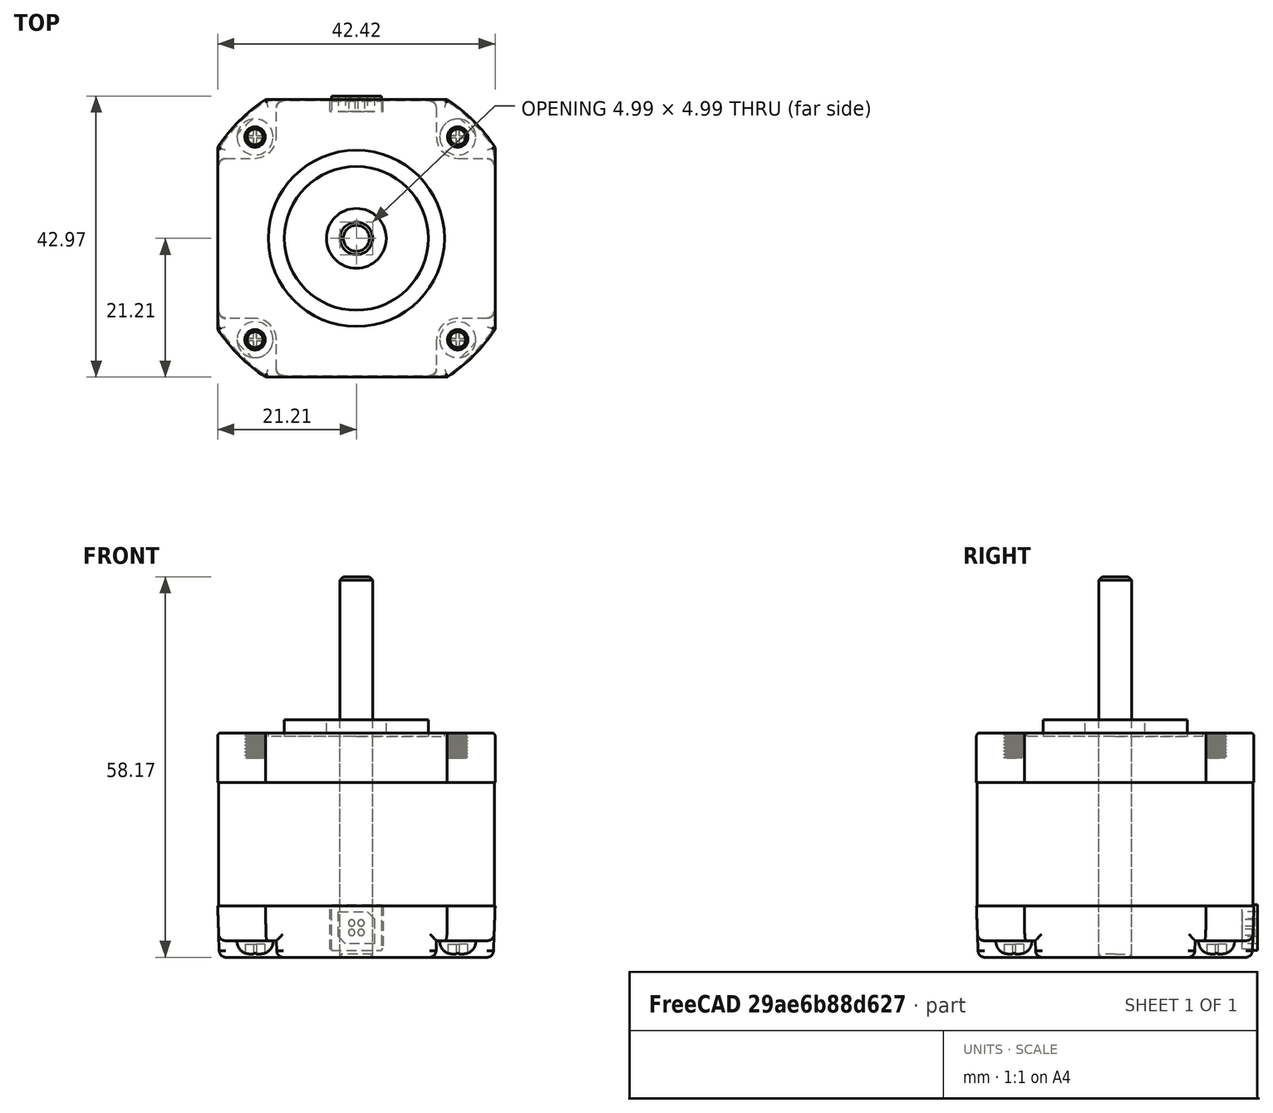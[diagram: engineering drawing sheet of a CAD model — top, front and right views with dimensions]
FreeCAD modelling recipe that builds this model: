
FCSTD DOCUMENT  (FreeCAD 0.19R22960 (Git))
Label: Nema17
License: All rights reserved
LicenseURL: http://en.wikipedia.org/wiki/All_rights_reserved
objects: App::DocumentObjectGroup×2, PartDesign::CoordinateSystem×2, Part::Feature×2, App::FeaturePython×1, Part::Compound2×1, App::Part×1
note: 4 computed .brp shape members not serialized (recipe doc carries the construction recipe); baked Part::Feature solids carry a one-line shape summary decoded from their .brp

FEATURE [App::DocumentObjectGroup] Parts
FEATURE [PartDesign::CoordinateSystem] LCS_Origin
  AttacherType = Attacher::AttachEngine3D
  MapMode = 2
  Support = -> [X_Axis]
FEATURE [App::DocumentObjectGroup] Constraints
FEATURE [App::FeaturePython] Variables  # WARN: FeaturePython — macro-defined, semantics opaque (R4)
FEATURE [Part::Feature] Solid
  shape: bbox 4.991 x 4.991 x 58.17 mm, 8 faces (baked)
FEATURE [Part::Feature] Solid001
  shape: bbox 45.91 x 45.91 x 36.32 mm, 325 faces (baked)
FEATURE [Part::Compound2] Compound  label="6627T66"
  Links = -> [Solid,Solid001]
FEATURE [PartDesign::CoordinateSystem] LCS_1
  AttacherType = Attacher::AttachEngine3D
  MapMode = 5
  Support = -> [Compound]
FEATURE [App::Part] Model
  Configuration = 0
  Group = -> [LCS_Origin,Constraints,Variables,LCS_1,Solid001,Solid,Compound]
  Origin = -> Origin
  Type = Assembly4 Model
